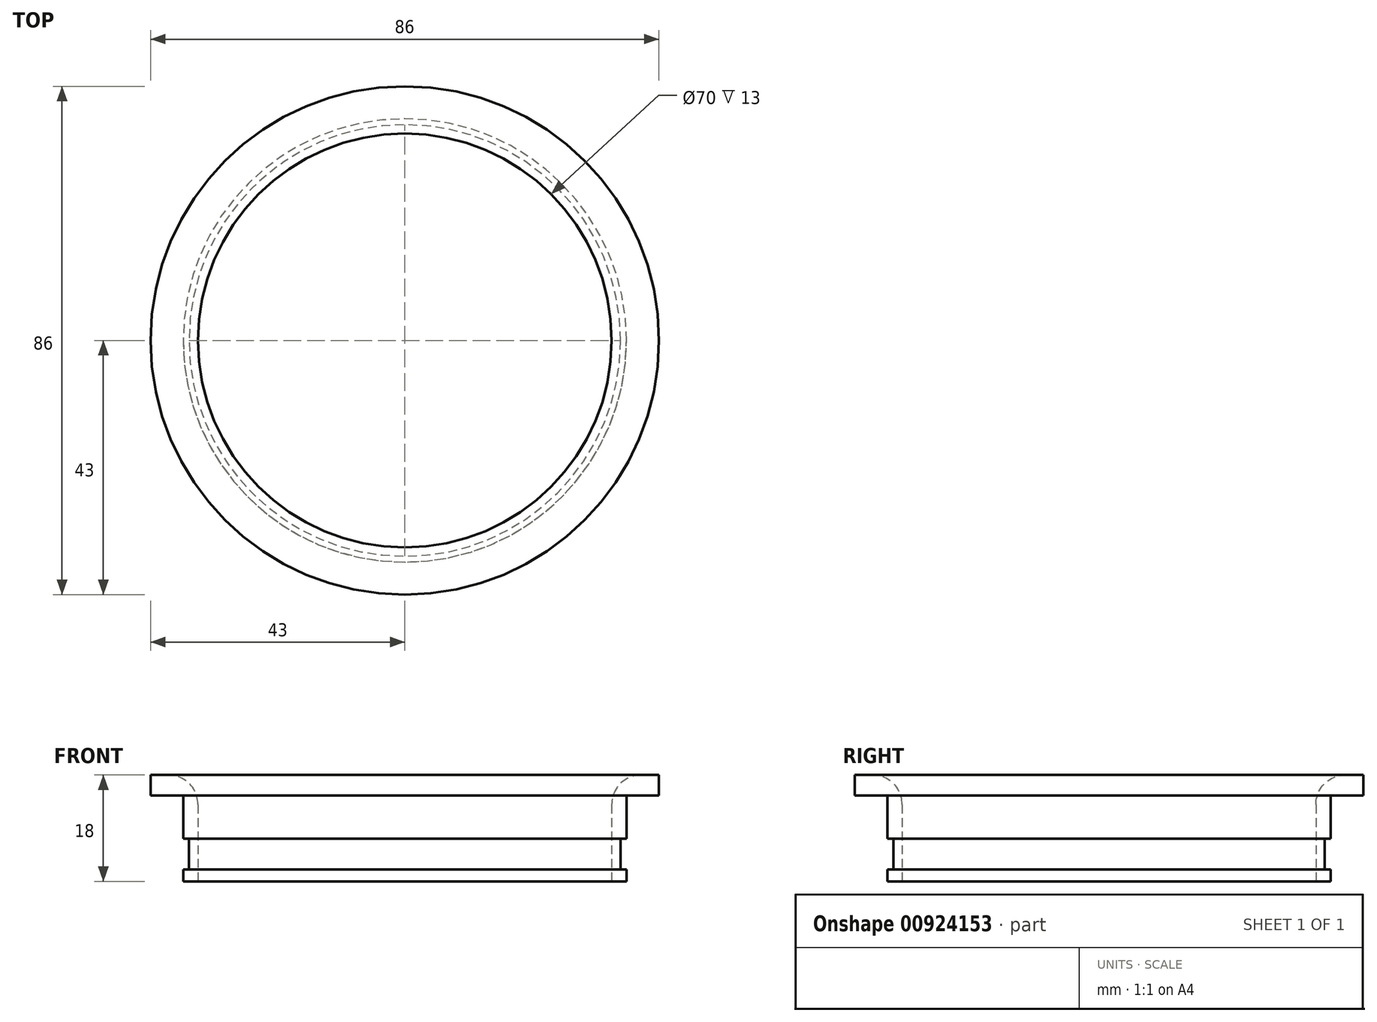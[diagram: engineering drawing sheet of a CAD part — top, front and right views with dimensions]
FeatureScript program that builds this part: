
annotation { "Feature Type Name" : "Feature", "Feature Type Description" : "" }
export const myFeature = defineFeature(function(context is Context, id is Id, definition is map)
    precondition{}
    {
        {
            var Q0;
            Q0=qCreatedBy(makeId("Top.planeOp"),FACE);
            var sketch = newSketch(context, id + "F0", { "sketchPlane" : qUnion([Q0])});
            skCircle(sketch, "E0", {"center": v(0, 0) * mm, "radius": 35 * mm});
            skCircle(sketch, "E1", {"center": v(0, 0) * mm, "radius": 37.5 * mm});
            skSolve(sketch);
        }
        {
            var Q0;
            Q0=makeQuery(id+"F0.imprint","IMPRINT",FACE,{"disambiguationData":[TD([[makeQuery(id+"F0.imprint","IMPRINT",EDGE,{"derivedFrom":sQuery(id+"F0.wireOp",EDGE,"E0")}),-1.0]])]});
            extrude(context, id + "F1", {"entities" : qUnion([Q0]), "depth" : 18 * mm, "offsetDistance" : 25 * mm});
        }
        {
            var Q0;
            Q0=makeQuery(id+"F1.opExtrude","CAP_FACE",FACE,{"disambiguationData":[OSD([sQuery(id+"F0.wireOp",EDGE,"E0"),sQuery(id+"F0.wireOp",EDGE,"E1")])],"isStart":false});
            var sketch = newSketch(context, id + "F2", { "sketchPlane" : qUnion([Q0])});
            skCircle(sketch, "E2", {"center": v(0, 0) * mm, "radius": 43 * mm});
            skCircle(sketch, "E3", {"center": v(0, 0) * mm, "radius": 35 * mm});
            skSolve(sketch);
        }
        {
            var Q0;
            Q0 = qSketchRegion(id + "F2", true);
            extrude(context, id + "F3", {"entities" : qUnion([Q0]), "operationType" : NewBodyOperationType.ADD, "oppositeDirection" : true, "depth" : 3.5 * mm, "offsetDistance" : 25 * mm});
        }
        {
            var Q0;
            Q0=makeQuery(id+"F1.opExtrude","CAP_EDGE",EDGE,{"disambiguationData":[OSD([sQuery(id+"F0.wireOp",EDGE,"E0")])],"isStart":false});
            fillet(context, id + "F4", {"entities" : qUnion([Q0]), "radius" : 5 * mm, "tangentPropagation" : true, "allowEdgeOverflow" : false});
        }
        {
            var Q0;
            Q0=makeQuery(id+"F1.opExtrude","CAP_FACE",FACE,{"disambiguationData":[OSD([sQuery(id+"F0.wireOp",EDGE,"E0"),sQuery(id+"F0.wireOp",EDGE,"E1")])],"isStart":true});
            cPlane(context, id + "F5", {"entities" : qUnion([Q0]), "cplaneType" : CPlaneType.OFFSET, "offset" : 2 * mm, "oppositeDirection" : true, "width" : 150 * mm, "height" : 150 * mm});
        }
        {
            var Q0;
            Q0=qCreatedBy(id+"F5.planeOp",FACE);
            var sketch = newSketch(context, id + "F6", { "sketchPlane" : qUnion([Q0])});
            skCircle(sketch, "E4", {"center": v(0, 0) * mm, "radius": 37.5 * mm});
            skCircle(sketch, "E5", {"center": v(0, 0) * mm, "radius": 36.5 * mm});
            skSolve(sketch);
        }
        {
            var Q0;
            Q0 = qSketchRegion(id + "F6", true);
            extrude(context, id + "F7", {"entities" : qUnion([Q0]), "operationType" : NewBodyOperationType.REMOVE, "oppositeDirection" : true, "depth" : 5.2 * mm, "offsetDistance" : 25 * mm});
        }
    });
